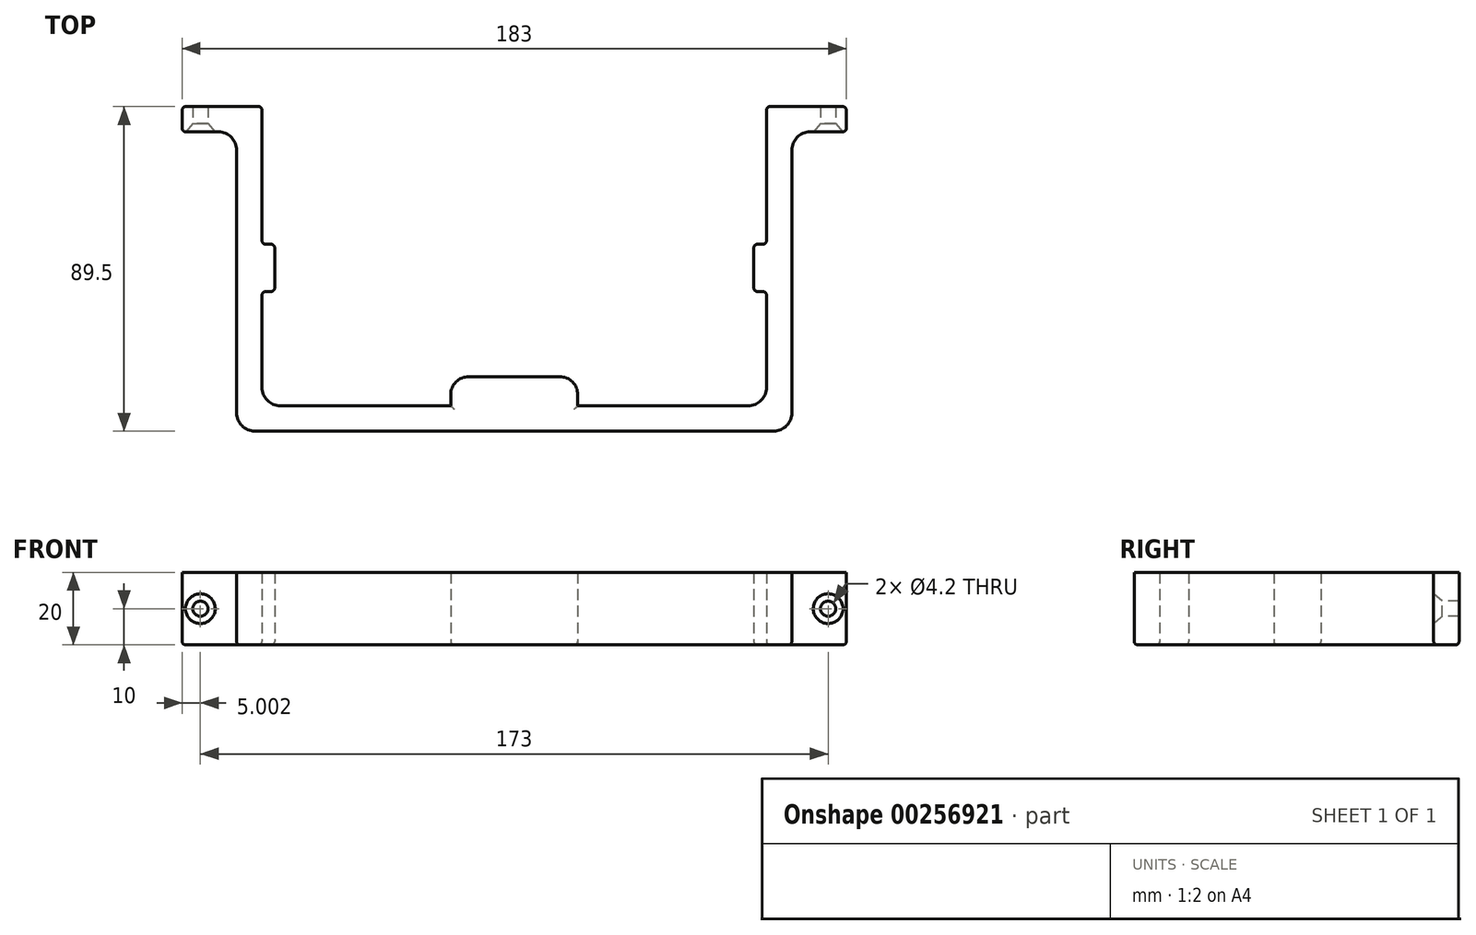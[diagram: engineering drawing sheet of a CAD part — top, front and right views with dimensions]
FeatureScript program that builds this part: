
annotation { "Feature Type Name" : "Feature", "Feature Type Description" : "" }
export const myFeature = defineFeature(function(context is Context, id is Id, definition is map)
    precondition{}
    {
        {
            var Q0;
            Q0=qCreatedBy(makeId("Top.planeOp"),FACE);
            var sketch = newSketch(context, id + "F0", { "sketchPlane" : qUnion([Q0])});
            skLineSegment(sketch, "E0.right", {"start": v(-22.03, -40.7) * mm, "end": v(-22.03, -48.7) * mm, "construction": true});
            skLineSegment(sketch, "E1.left", {"start": v(-70.53, -17.2) * mm, "end": v(-70.53, -10.7) * mm, "construction": true});
            skLineSegment(sketch, "E2", {"start": v(-70.53, -17.2) * mm, "end": v(-70.53, -4.2) * mm});
            skLineSegment(sketch, "E3", {"start": v(-4.53, -40.7) * mm, "end": v(-4.53, 33.8) * mm, "construction": true});
            skLineSegment(sketch, "E4", {"start": v(-74.03, -48.7) * mm, "end": v(-74.03, -40.7) * mm, "construction": true});
            skLineSegment(sketch, "E5", {"start": v(-70.53, -4.2) * mm, "end": v(-74.03, -4.2) * mm, "construction": true});
            skLineSegment(sketch, "E6", {"start": v(-4.53, -40.7) * mm, "end": v(-17.03, -40.7) * mm});
            skLineSegment(sketch, "E7", {"start": v(-22.03, -48.7) * mm, "end": v(-74.03, -48.7) * mm});
            skLineSegment(sketch, "E8", {"start": v(-74.03, -48.7) * mm, "end": v(-74.03, -17.2) * mm});
            skLineSegment(sketch, "E9", {"start": v(-74.03, -17.2) * mm, "end": v(-70.53, -17.2) * mm});
            skLineSegment(sketch, "E10", {"start": v(-70.53, -4.2) * mm, "end": v(-74.03, -4.2) * mm});
            skLineSegment(sketch, "E11", {"start": v(-74.03, -4.2) * mm, "end": v(-74.03, 33.8) * mm});
            skLineSegment(sketch, "E12.MirrorCS", {"start": v(61.47, -4.2) * mm, "end": v(64.97, -4.2) * mm});
            skLineSegment(sketch, "E13.MirrorCS", {"start": v(61.47, -4.2) * mm, "end": v(64.97, -4.2) * mm, "construction": true});
            skLineSegment(sketch, "E14.MirrorCS", {"start": v(64.97, -17.2) * mm, "end": v(61.47, -17.2) * mm});
            skLineSegment(sketch, "E15.MirrorCS", {"start": v(-4.53, -40.7) * mm, "end": v(7.97, -40.7) * mm});
            skLineSegment(sketch, "E16.MirrorCS", {"start": v(61.47, -17.2) * mm, "end": v(61.47, -4.2) * mm});
            skLineSegment(sketch, "E17.MirrorCS", {"start": v(64.97, -4.2) * mm, "end": v(64.97, 33.8) * mm});
            skLineSegment(sketch, "E18.MirrorCS", {"start": v(64.97, -48.7) * mm, "end": v(64.97, -17.2) * mm});
            skLineSegment(sketch, "E19.MirrorCS", {"start": v(12.97, -48.7) * mm, "end": v(64.97, -48.7) * mm});
            skLineSegment(sketch, "E20.MirrorCS", {"start": v(61.47, -17.2) * mm, "end": v(61.47, -4.2) * mm, "construction": true});
            skLineSegment(sketch, "E21.MirrorCS", {"start": v(64.97, -4.2) * mm, "end": v(64.97, 33.8) * mm, "construction": true});
            skLineSegment(sketch, "E22", {"start": v(-22.03, -45.7) * mm, "end": v(-22.03, -48.7) * mm});
            skLineSegment(sketch, "E23", {"start": v(12.97, -45.7) * mm, "end": v(12.97, -48.7) * mm});
            skLineSegment(sketch, "E24", {"start": v(-74.03, 33.8) * mm, "end": v(-81.03, 33.8) * mm});
            skLineSegment(sketch, "E25", {"start": v(-81.03, 21.8) * mm, "end": v(-81.03, -48.7) * mm});
            skLineSegment(sketch, "E26", {"start": v(-48.03, -55.7) * mm, "end": v(-76.03, -55.7) * mm});
            skLineSegment(sketch, "E27", {"start": v(-81.03, -50.7) * mm, "end": v(-81.03, -48.7) * mm});
            skLineSegment(sketch, "E28", {"start": v(-48.03, -55.7) * mm, "end": v(-4.53, -55.7) * mm});
            skLineSegment(sketch, "E29.MirrorCS", {"start": v(64.97, 33.8) * mm, "end": v(71.97, 33.8) * mm});
            skLineSegment(sketch, "E30.MirrorCS", {"start": v(71.97, 21.8) * mm, "end": v(71.97, -48.7) * mm});
            skLineSegment(sketch, "E31.MirrorCS", {"start": v(71.97, -50.7) * mm, "end": v(71.97, -48.7) * mm});
            skLineSegment(sketch, "E32.MirrorCS", {"start": v(38.97, -55.7) * mm, "end": v(-4.53, -55.7) * mm});
            skLineSegment(sketch, "E33.MirrorCS", {"start": v(38.97, -55.7) * mm, "end": v(66.97, -55.7) * mm});
            skLineSegment(sketch, "E34", {"start": v(-81.03, 33.8) * mm, "end": v(-96.03, 33.8) * mm});
            skLineSegment(sketch, "E35", {"start": v(-96.03, 33.8) * mm, "end": v(-96.03, 26.8) * mm});
            skLineSegment(sketch, "E36", {"start": v(-96.03, 26.8) * mm, "end": v(-86.03, 26.8) * mm});
            skLineSegment(sketch, "E37.MirrorCS", {"start": v(86.97, 26.8) * mm, "end": v(76.97, 26.8) * mm});
            skLineSegment(sketch, "E38.MirrorCS", {"start": v(86.97, 33.8) * mm, "end": v(86.97, 26.8) * mm});
            skLineSegment(sketch, "E39.MirrorCS", {"start": v(71.97, 33.8) * mm, "end": v(86.97, 33.8) * mm});
            skPoint(sketch, "E40.visualSharp", {"position": v(-81.03, 26.8) * mm});
            skArc(sketch, "E40.filletArc", {"start": v(-81.03, 21.8) * mm, "mid": v(-82.5, 25.33) * mm, "end": v(-86.03, 26.8) * mm});
            skPoint(sketch, "E41.visualSharp", {"position": v(71.97, 26.8) * mm});
            skArc(sketch, "E41.filletArc", {"start": v(76.97, 26.8) * mm, "mid": v(73.44, 25.33) * mm, "end": v(71.97, 21.8) * mm});
            skPoint(sketch, "E42.visualSharp", {"position": v(-81.03, -55.7) * mm});
            skArc(sketch, "E42.filletArc", {"start": v(-81.03, -50.7) * mm, "mid": v(-79.56, -54.24) * mm, "end": v(-76.03, -55.7) * mm});
            skPoint(sketch, "E43.visualSharp", {"position": v(71.97, -55.7) * mm});
            skArc(sketch, "E43.filletArc", {"start": v(66.97, -55.7) * mm, "mid": v(70.5, -54.24) * mm, "end": v(71.97, -50.7) * mm});
            skPoint(sketch, "E44.visualSharp", {"position": v(-22.03, -40.7) * mm});
            skArc(sketch, "E44.filletArc", {"start": v(-17.03, -40.7) * mm, "mid": v(-20.56, -42.17) * mm, "end": v(-22.03, -45.7) * mm});
            skPoint(sketch, "E45.visualSharp", {"position": v(12.97, -40.7) * mm});
            skArc(sketch, "E45.filletArc", {"start": v(12.97, -45.7) * mm, "mid": v(11.5, -42.17) * mm, "end": v(7.97, -40.7) * mm});
            skSolve(sketch);
        }
        {
            var Q0;
            Q0=makeQuery(id+"F0.imprint","IMPRINT",FACE,{"disambiguationData":[TD([[makeQuery(id+"F0.imprint","IMPRINT",EDGE,{"derivedFrom":sQuery(id+"F0.wireOp",EDGE,"E2")}),1.0]])]});
            extrude(context, id + "F1", {"entities" : qUnion([Q0]), "depth" : 20 * mm});
        }
        {
            var Q0;
            Q0=makeQuery(id+"F1.opExtrude","SWEPT_FACE",FACE,{"disambiguationData":[OSD([sQuery(id+"F0.wireOp",EDGE,"E36")])]});
            var sketch = newSketch(context, id + "F2", { "sketchPlane" : qUnion([Q0])});
            skPoint(sketch, "E46", {"position": v(-91.03, 10) * mm});
            skPoint(sketch, "E46.positionSnap0", {"position": v(-91.03, 0) * mm});
            skPoint(sketch, "E46.positionSnap1", {"position": v(-96.03, 10) * mm});
            skSolve(sketch);
        }
        {
            var Q0;
            Q0=makeQuery(id+"F1.opExtrude","SWEPT_FACE",FACE,{"disambiguationData":[OSD([sQuery(id+"F0.wireOp",EDGE,"E37.MirrorCS")])]});
            var sketch = newSketch(context, id + "F3", { "sketchPlane" : qUnion([Q0])});
            skPoint(sketch, "E47", {"position": v(81.97, 10) * mm});
            skPoint(sketch, "E47.positionSnap0", {"position": v(86.97, 10) * mm});
            skPoint(sketch, "E47.positionSnap1", {"position": v(81.97, 20) * mm});
            skSolve(sketch);
        }
        {
            var Q0;
            Q0=sQuery(id+"F3.wireOp",VERTEX,"E47");
            var Q1;
            Q1=sQuery(id+"F2.wireOp",VERTEX,"E46");
            var Q2;
            Q2=makeQuery(id+"F1.opExtrude","SWEPT_BODY",BODY,{"disambiguationData":[OSD([sQuery(id+"F0.wireOp",EDGE,"E2"),sQuery(id+"F0.wireOp",EDGE,"E6"),sQuery(id+"F0.wireOp",EDGE,"E7"),sQuery(id+"F0.wireOp",EDGE,"E8"),sQuery(id+"F0.wireOp",EDGE,"E9"),sQuery(id+"F0.wireOp",EDGE,"E10"),sQuery(id+"F0.wireOp",EDGE,"E11"),sQuery(id+"F0.wireOp",EDGE,"E12.MirrorCS"),sQuery(id+"F0.wireOp",EDGE,"E14.MirrorCS"),sQuery(id+"F0.wireOp",EDGE,"E15.MirrorCS"),sQuery(id+"F0.wireOp",EDGE,"E16.MirrorCS"),sQuery(id+"F0.wireOp",EDGE,"E17.MirrorCS"),sQuery(id+"F0.wireOp",EDGE,"E18.MirrorCS"),sQuery(id+"F0.wireOp",EDGE,"E19.MirrorCS"),sQuery(id+"F0.wireOp",EDGE,"E22"),sQuery(id+"F0.wireOp",EDGE,"E23"),sQuery(id+"F0.wireOp",EDGE,"E24"),sQuery(id+"F0.wireOp",EDGE,"E25"),sQuery(id+"F0.wireOp",EDGE,"E26"),sQuery(id+"F0.wireOp",EDGE,"E27"),sQuery(id+"F0.wireOp",EDGE,"E28"),sQuery(id+"F0.wireOp",EDGE,"E30.MirrorCS"),sQuery(id+"F0.wireOp",EDGE,"E31.MirrorCS"),sQuery(id+"F0.wireOp",EDGE,"E32.MirrorCS"),sQuery(id+"F0.wireOp",EDGE,"E33.MirrorCS"),sQuery(id+"F0.wireOp",EDGE,"E34"),sQuery(id+"F0.wireOp",EDGE,"E35"),sQuery(id+"F0.wireOp",EDGE,"E36"),sQuery(id+"F0.wireOp",EDGE,"E37.MirrorCS"),sQuery(id+"F0.wireOp",EDGE,"E38.MirrorCS"),sQuery(id+"F0.wireOp",EDGE,"E29.MirrorCS"),sQuery(id+"F0.wireOp",EDGE,"E39.MirrorCS"),sQuery(id+"F0.wireOp",EDGE,"E40.filletArc"),sQuery(id+"F0.wireOp",EDGE,"E41.filletArc"),sQuery(id+"F0.wireOp",EDGE,"E42.filletArc"),sQuery(id+"F0.wireOp",EDGE,"E43.filletArc"),sQuery(id+"F0.wireOp",EDGE,"E44.filletArc"),sQuery(id+"F0.wireOp",EDGE,"E45.filletArc")])]});
            hole(context, id + "F4", {"style" : HoleStyle.C_SINK, "endStyle" : HoleEndStyle.THROUGH, "holeDiameter" : 4.2 * mm, "cSinkDiameter" : 8.2 * mm, "cSinkAngle" : 80 * degree, "tappedDepth" : 12 * mm, "tapClearance" : 3, "startFromSketch" : true, "locations" : qUnion([Q0, Q1]), "scope" : qUnion([Q2])});
        }
        {
            var Q0;
            Q0=makeQuery(id+"F1.opExtrude","SWEPT_EDGE",EDGE,{"disambiguationData":[OSD([sQuery(id+"F0.wireOp",EDGE,"E17.MirrorCS"),sQuery(id+"F0.wireOp",EDGE,"E29.MirrorCS")])]});
            var Q1;
            Q1=makeQuery(id+"F1.opExtrude","SWEPT_EDGE",EDGE,{"disambiguationData":[OSD([sQuery(id+"F0.wireOp",EDGE,"E12.MirrorCS"),sQuery(id+"F0.wireOp",EDGE,"E16.MirrorCS")])]});
            var Q2;
            Q2=makeQuery(id+"F1.opExtrude","SWEPT_EDGE",EDGE,{"disambiguationData":[OSD([sQuery(id+"F0.wireOp",EDGE,"E14.MirrorCS"),sQuery(id+"F0.wireOp",EDGE,"E16.MirrorCS")])]});
            var Q3;
            Q3=makeQuery(id+"F1.opExtrude","SWEPT_EDGE",EDGE,{"disambiguationData":[OSD([sQuery(id+"F0.wireOp",EDGE,"E10"),sQuery(id+"F0.wireOp",EDGE,"E11")])]});
            var Q4;
            Q4=makeQuery(id+"F1.opExtrude","SWEPT_EDGE",EDGE,{"disambiguationData":[OSD([sQuery(id+"F0.wireOp",EDGE,"E2"),sQuery(id+"F0.wireOp",EDGE,"E9")])]});
            var Q5;
            Q5=makeQuery(id+"F1.opExtrude","SWEPT_EDGE",EDGE,{"disambiguationData":[OSD([sQuery(id+"F0.wireOp",EDGE,"E11"),sQuery(id+"F0.wireOp",EDGE,"E24")])]});
            var Q6;
            Q6=makeQuery(id+"F1.opExtrude","SWEPT_EDGE",EDGE,{"disambiguationData":[OSD([sQuery(id+"F0.wireOp",EDGE,"E37.MirrorCS"),sQuery(id+"F0.wireOp",EDGE,"E38.MirrorCS")])]});
            var Q7;
            Q7=makeQuery(id+"F1.opExtrude","SWEPT_EDGE",EDGE,{"disambiguationData":[OSD([sQuery(id+"F0.wireOp",EDGE,"E38.MirrorCS"),sQuery(id+"F0.wireOp",EDGE,"E39.MirrorCS")])]});
            var Q8;
            Q8=makeQuery(id+"F1.opExtrude","SWEPT_EDGE",EDGE,{"disambiguationData":[OSD([sQuery(id+"F0.wireOp",EDGE,"E2"),sQuery(id+"F0.wireOp",EDGE,"E10")])]});
            var Q9;
            Q9=makeQuery(id+"F1.opExtrude","SWEPT_EDGE",EDGE,{"disambiguationData":[OSD([sQuery(id+"F0.wireOp",EDGE,"E8"),sQuery(id+"F0.wireOp",EDGE,"E9")])]});
            var Q10;
            Q10=makeQuery(id+"F1.opExtrude","SWEPT_EDGE",EDGE,{"disambiguationData":[OSD([sQuery(id+"F0.wireOp",EDGE,"E14.MirrorCS"),sQuery(id+"F0.wireOp",EDGE,"E18.MirrorCS")])]});
            var Q11;
            Q11=makeQuery(id+"F1.opExtrude","SWEPT_EDGE",EDGE,{"disambiguationData":[OSD([sQuery(id+"F0.wireOp",EDGE,"E12.MirrorCS"),sQuery(id+"F0.wireOp",EDGE,"E17.MirrorCS")])]});
            var Q12;
            Q12=makeQuery(id+"F1.opExtrude","SWEPT_EDGE",EDGE,{"disambiguationData":[OSD([sQuery(id+"F0.wireOp",EDGE,"E34"),sQuery(id+"F0.wireOp",EDGE,"E35")])]});
            var Q13;
            Q13=makeQuery(id+"F1.opExtrude","SWEPT_EDGE",EDGE,{"disambiguationData":[OSD([sQuery(id+"F0.wireOp",EDGE,"E35"),sQuery(id+"F0.wireOp",EDGE,"E36")])]});
            fillet(context, id + "F5", {"entities" : qUnion([Q0, Q1, Q2, Q3, Q4, Q5, Q6, Q7, Q8, Q9, Q10, Q11, Q12, Q13]), "radius" : 1 * mm, "tangentPropagation" : true, "allowEdgeOverflow" : false});
        }
        {
            var Q0;
            Q0=makeQuery(id+"F1.opExtrude","SWEPT_EDGE",EDGE,{"disambiguationData":[OSD([sQuery(id+"F0.wireOp",EDGE,"E18.MirrorCS"),sQuery(id+"F0.wireOp",EDGE,"E19.MirrorCS")])]});
            var Q1;
            Q1=makeQuery(id+"F1.opExtrude","SWEPT_EDGE",EDGE,{"disambiguationData":[OSD([sQuery(id+"F0.wireOp",EDGE,"E7"),sQuery(id+"F0.wireOp",EDGE,"E8")])]});
            fillet(context, id + "F6", {"entities" : qUnion([Q0, Q1]), "radius" : 5 * mm, "tangentPropagation" : true, "allowEdgeOverflow" : false});
        }
        {
            var Q0;
            Q0=makeQuery(id+"F1.opExtrude","CAP_FACE",FACE,{"disambiguationData":[OSD([sQuery(id+"F0.wireOp",EDGE,"E2"),sQuery(id+"F0.wireOp",EDGE,"E6"),sQuery(id+"F0.wireOp",EDGE,"E7"),sQuery(id+"F0.wireOp",EDGE,"E8"),sQuery(id+"F0.wireOp",EDGE,"E9"),sQuery(id+"F0.wireOp",EDGE,"E10"),sQuery(id+"F0.wireOp",EDGE,"E11"),sQuery(id+"F0.wireOp",EDGE,"E12.MirrorCS"),sQuery(id+"F0.wireOp",EDGE,"E14.MirrorCS"),sQuery(id+"F0.wireOp",EDGE,"E15.MirrorCS"),sQuery(id+"F0.wireOp",EDGE,"E16.MirrorCS"),sQuery(id+"F0.wireOp",EDGE,"E17.MirrorCS"),sQuery(id+"F0.wireOp",EDGE,"E18.MirrorCS"),sQuery(id+"F0.wireOp",EDGE,"E19.MirrorCS"),sQuery(id+"F0.wireOp",EDGE,"E22"),sQuery(id+"F0.wireOp",EDGE,"E23"),sQuery(id+"F0.wireOp",EDGE,"E24"),sQuery(id+"F0.wireOp",EDGE,"E25"),sQuery(id+"F0.wireOp",EDGE,"E26"),sQuery(id+"F0.wireOp",EDGE,"E27"),sQuery(id+"F0.wireOp",EDGE,"E28"),sQuery(id+"F0.wireOp",EDGE,"E30.MirrorCS"),sQuery(id+"F0.wireOp",EDGE,"E31.MirrorCS"),sQuery(id+"F0.wireOp",EDGE,"E32.MirrorCS"),sQuery(id+"F0.wireOp",EDGE,"E33.MirrorCS"),sQuery(id+"F0.wireOp",EDGE,"E34"),sQuery(id+"F0.wireOp",EDGE,"E35"),sQuery(id+"F0.wireOp",EDGE,"E36"),sQuery(id+"F0.wireOp",EDGE,"E37.MirrorCS"),sQuery(id+"F0.wireOp",EDGE,"E38.MirrorCS"),sQuery(id+"F0.wireOp",EDGE,"E29.MirrorCS"),sQuery(id+"F0.wireOp",EDGE,"E39.MirrorCS"),sQuery(id+"F0.wireOp",EDGE,"E40.filletArc"),sQuery(id+"F0.wireOp",EDGE,"E41.filletArc"),sQuery(id+"F0.wireOp",EDGE,"E42.filletArc"),sQuery(id+"F0.wireOp",EDGE,"E43.filletArc"),sQuery(id+"F0.wireOp",EDGE,"E44.filletArc"),sQuery(id+"F0.wireOp",EDGE,"E45.filletArc")])],"isStart":true});
            fillet(context, id + "F7", {"entities" : qUnion([Q0]), "radius" : 1 * mm, "tangentPropagation" : true, "allowEdgeOverflow" : false});
        }
    });
